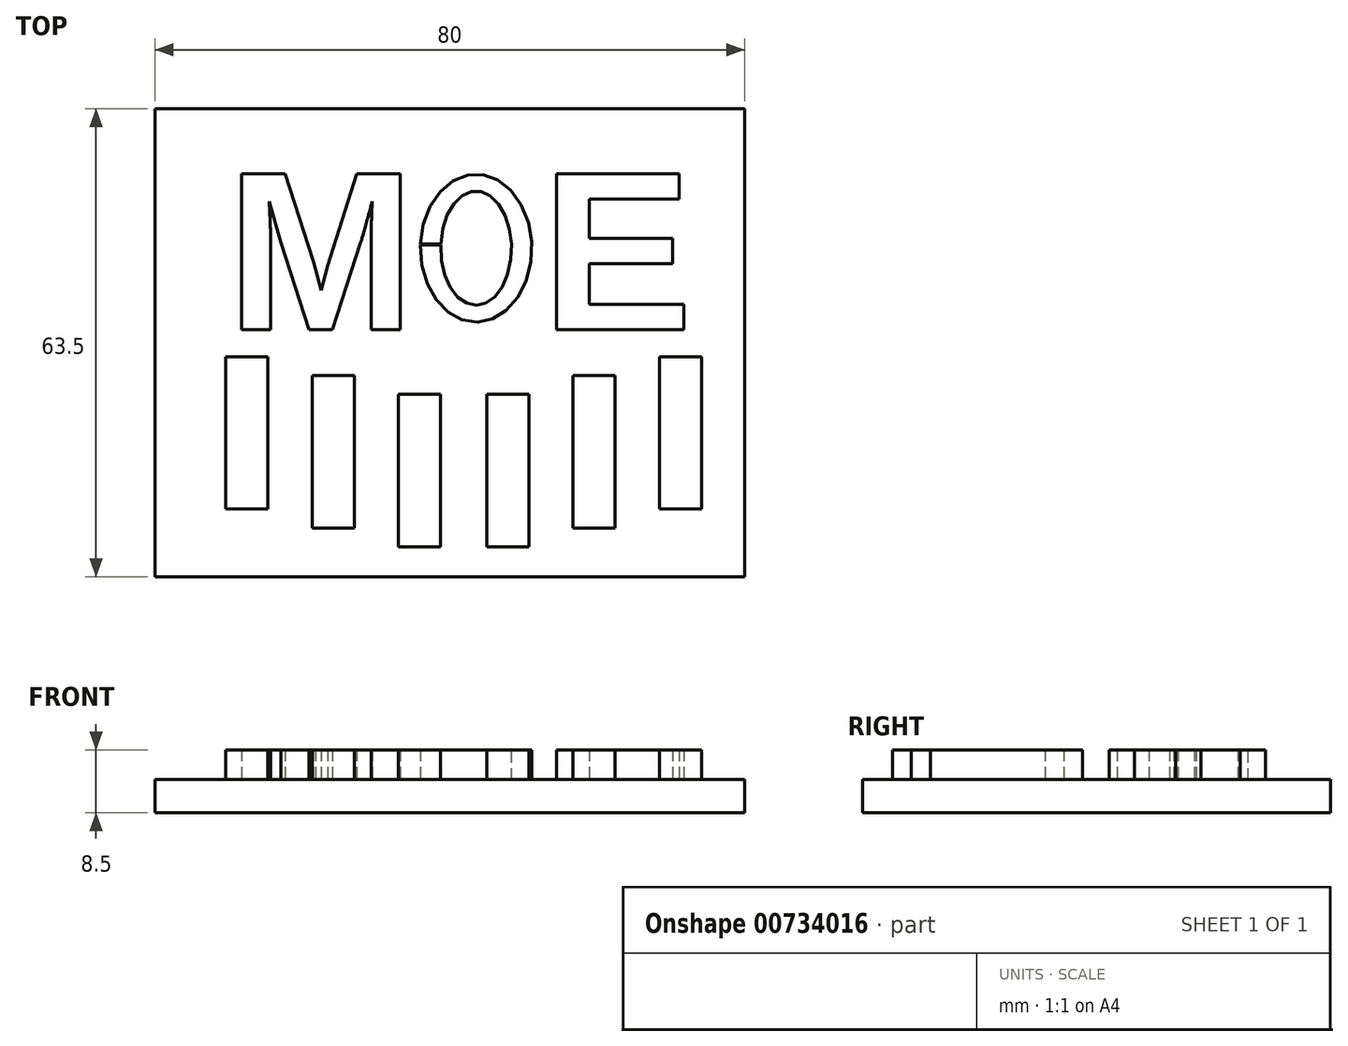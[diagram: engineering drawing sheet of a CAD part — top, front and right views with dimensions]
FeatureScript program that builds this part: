
annotation { "Feature Type Name" : "Feature", "Feature Type Description" : "" }
export const myFeature = defineFeature(function(context is Context, id is Id, definition is map)
    precondition{}
    {
        {
            var Q0;
            Q0=qCreatedBy(makeId("Top.planeOp"),FACE);
            var sketch = newSketch(context, id + "F0", { "sketchPlane" : qUnion([Q0])});
            skLineSegment(sketch, "E0.bottom", {"start": v(40, -33.5) * mm, "end": v(-40, -33.5) * mm});
            skLineSegment(sketch, "E0.top", {"start": v(40, 30) * mm, "end": v(-40, 30) * mm});
            skLineSegment(sketch, "E0.left", {"start": v(40, -30) * mm, "end": v(40, 30) * mm});
            skLineSegment(sketch, "E0.right", {"start": v(-40, -30) * mm, "end": v(-40, 30) * mm});
            skPoint(sketch, "E0.middle", {"position": v(0, 0) * mm});
            skLineSegment(sketch, "E1", {"start": v(-40, -32.5) * mm, "end": v(-40, -30) * mm});
            skLineSegment(sketch, "E2", {"start": v(40, -32.5) * mm, "end": v(40, -30) * mm});
            skLineSegment(sketch, "E3", {"start": v(-40, -33.5) * mm, "end": v(-40, -32.5) * mm});
            skLineSegment(sketch, "E4", {"start": v(40, -33.5) * mm, "end": v(40, -32.5) * mm});
            skSolve(sketch);
        }
        {
            var Q0;
            Q0=qCreatedBy(makeId("Top.planeOp"),FACE);
            var sketch = newSketch(context, id + "F1", { "sketchPlane" : qUnion([Q0])});
            skLineSegment(sketch, "E5.bottom", {"start": v(37, 29.06) * mm, "end": v(-37, 29.06) * mm});
            skLineSegment(sketch, "E5.top", {"start": v(37, -33.44) * mm, "end": v(-37, -33.44) * mm});
            skLineSegment(sketch, "E5.left", {"start": v(39.5, 29.06) * mm, "end": v(39.5, -30.94) * mm});
            skLineSegment(sketch, "E5.right", {"start": v(-39.5, 29.06) * mm, "end": v(-39.5, -30.94) * mm});
            skEllipticalArc(sketch, "E6", {});
            skEllipticalArc(sketch, "E7", {});
            skLineSegment(sketch, "E8", {"start": v(-4, 11.66) * mm, "end": v(-1.23, 11.66) * mm});
            skLineSegment(sketch, "E9", {"start": v(-4, 11.5) * mm, "end": v(-1.24, 11.5) * mm});
            skPoint(sketch, "E10", {"position": v(-2.7, -4.34) * mm});
            skLineSegment(sketch, "E11", {"start": v(-39.5, 29.06) * mm, "end": v(-37, 29.06) * mm});
            skLineSegment(sketch, "E12", {"start": v(37, 29.06) * mm, "end": v(39.5, 29.06) * mm});
            skLineSegment(sketch, "E13", {"start": v(39.5, -30.94) * mm, "end": v(39.5, -33.44) * mm});
            skLineSegment(sketch, "E14", {"start": v(39.5, -33.44) * mm, "end": v(37, -33.44) * mm});
            skLineSegment(sketch, "E15", {"start": v(-39.5, -30.94) * mm, "end": v(-39.5, -33.44) * mm});
            skLineSegment(sketch, "E16", {"start": v(-39.5, -33.44) * mm, "end": v(-37, -33.44) * mm});
            skText(sketch, "E17", { "text": "M  E", "fontName": "Arimo-Bold.ttf"});
            skLineSegment(sketch, "E18.bottom", {"start": v(-24.68, -24.3) * mm, "end": v(-30.4, -24.3) * mm});
            skLineSegment(sketch, "E18.top", {"start": v(-24.68, -3.67) * mm, "end": v(-30.4, -3.67) * mm});
            skLineSegment(sketch, "E18.left", {"start": v(-24.68, -24.3) * mm, "end": v(-24.68, -3.67) * mm});
            skLineSegment(sketch, "E18.right", {"start": v(-30.4, -24.3) * mm, "end": v(-30.4, -3.67) * mm});
            skPoint(sketch, "E18.middle", {"position": v(-27.54, -13.98) * mm});
            skLineSegment(sketch, "E19.bottom", {"start": v(-12.96, -26.9) * mm, "end": v(-18.68, -26.9) * mm});
            skLineSegment(sketch, "E19.top", {"start": v(-12.96, -6.17) * mm, "end": v(-18.68, -6.17) * mm});
            skLineSegment(sketch, "E19.left", {"start": v(-12.96, -26.9) * mm, "end": v(-12.96, -6.17) * mm});
            skLineSegment(sketch, "E19.right", {"start": v(-18.68, -26.9) * mm, "end": v(-18.68, -6.17) * mm});
            skPoint(sketch, "E19.middle", {"position": v(-15.82, -16.53) * mm});
            skLineSegment(sketch, "E20.bottom", {"start": v(-1.25, -29.45) * mm, "end": v(-6.96, -29.45) * mm});
            skLineSegment(sketch, "E20.top", {"start": v(-1.25, -8.73) * mm, "end": v(-6.96, -8.73) * mm});
            skLineSegment(sketch, "E20.left", {"start": v(-1.25, -29.45) * mm, "end": v(-1.25, -8.73) * mm});
            skLineSegment(sketch, "E20.right", {"start": v(-6.96, -29.45) * mm, "end": v(-6.96, -8.73) * mm});
            skPoint(sketch, "E20.middle", {"position": v(-4.1, -19.09) * mm});
            skLineSegment(sketch, "E21.MirrorCS", {"start": v(28.44, -3.67) * mm, "end": v(34.15, -3.67) * mm});
            skLineSegment(sketch, "E22.MirrorCS", {"start": v(28.44, -24.3) * mm, "end": v(28.44, -3.67) * mm});
            skPoint(sketch, "E23.MirrorP", {"position": v(6.46, -4.34) * mm});
            skLineSegment(sketch, "E24.MirrorCS", {"start": v(16.72, -26.9) * mm, "end": v(16.72, -6.17) * mm});
            skLineSegment(sketch, "E25.MirrorCS", {"start": v(5, -29.45) * mm, "end": v(5, -8.73) * mm});
            skLineSegment(sketch, "E26.MirrorCS", {"start": v(5, -8.73) * mm, "end": v(10.72, -8.73) * mm});
            skLineSegment(sketch, "E27.MirrorCS", {"start": v(16.72, -6.17) * mm, "end": v(22.44, -6.17) * mm});
            skLineSegment(sketch, "E28.MirrorCS", {"start": v(16.72, -26.9) * mm, "end": v(22.44, -26.9) * mm});
            skLineSegment(sketch, "E29.MirrorCS", {"start": v(22.44, -26.9) * mm, "end": v(22.44, -6.17) * mm});
            skPoint(sketch, "E30.MirrorP", {"position": v(19.58, -16.53) * mm});
            skLineSegment(sketch, "E31.MirrorCS", {"start": v(34.15, -24.3) * mm, "end": v(34.15, -3.67) * mm});
            skLineSegment(sketch, "E32.MirrorCS", {"start": v(10.72, -29.45) * mm, "end": v(10.72, -8.73) * mm});
            skLineSegment(sketch, "E33.MirrorCS", {"start": v(5, -29.45) * mm, "end": v(10.72, -29.45) * mm});
            skLineSegment(sketch, "E34.MirrorCS", {"start": v(28.44, -24.3) * mm, "end": v(34.15, -24.3) * mm});
            skPoint(sketch, "E35.MirrorP", {"position": v(7.86, -19.09) * mm});
            skPoint(sketch, "E36.MirrorP", {"position": v(31.3, -13.98) * mm});
            const initialGuessF1  = {"E6": [0.0035593705279581347, 0.011075022630393505, 0, -1, 0.010015109553933144, 0.007566245832075456, 4.669752922945587, 4.654139303713688], "E7": [0.0035593705279581347, 0.011075022630393505, 0, -1, 0.007730962708592415, 0.0048037835103717265, 4.657144549083569, 4.636900170979201], "E17": [-0.03033, 0, 1, 0, 0.02216]};
            skSetInitialGuess(sketch, initialGuessF1);
            skSolve(sketch);
        }
        {
            var Q0;
            Q0=makeQuery(id+"F1.imprint","IMPRINT",FACE,{"disambiguationData":[TD([[makeQuery(id+"F1.imprint","IMPRINT",EDGE,{"derivedFrom":sQuery(id+"F1.wireOp",EDGE,"E17.sketch_text.stroke-0")}),-1.0]])]});
            var Q1;
            Q1=makeQuery(id+"F1.imprint","IMPRINT",FACE,{"disambiguationData":[TD([[makeQuery(id+"F1.imprint","IMPRINT",EDGE,{"derivedFrom":sQuery(id+"F1.wireOp",EDGE,"E6")}),1.0]])]});
            var Q2;
            Q2=makeQuery(id+"F1.imprint","IMPRINT",FACE,{"disambiguationData":[TD([[makeQuery(id+"F1.imprint","IMPRINT",EDGE,{"derivedFrom":sQuery(id+"F1.wireOp",EDGE,"E17.sketch_text.stroke-21")}),-1.0]])]});
            var Q3;
            Q3=makeQuery(id+"F1.imprint","IMPRINT",FACE,{"disambiguationData":[TD([[makeQuery(id+"F1.imprint","IMPRINT",EDGE,{"derivedFrom":sQuery(id+"F1.wireOp",EDGE,"E18.bottom")}),-1.0]])]});
            var Q4;
            Q4=makeQuery(id+"F1.imprint","IMPRINT",FACE,{"disambiguationData":[TD([[makeQuery(id+"F1.imprint","IMPRINT",EDGE,{"derivedFrom":sQuery(id+"F1.wireOp",EDGE,"E19.bottom")}),-1.0]])]});
            var Q5;
            Q5=makeQuery(id+"F1.imprint","IMPRINT",FACE,{"disambiguationData":[TD([[makeQuery(id+"F1.imprint","IMPRINT",EDGE,{"derivedFrom":sQuery(id+"F1.wireOp",EDGE,"E20.bottom")}),-1.0]])]});
            var Q6;
            Q6=makeQuery(id+"F1.imprint","IMPRINT",FACE,{"disambiguationData":[TD([[makeQuery(id+"F1.imprint","IMPRINT",EDGE,{"derivedFrom":sQuery(id+"F1.wireOp",EDGE,"E25.MirrorCS")}),-1.0]])]});
            var Q7;
            Q7=makeQuery(id+"F1.imprint","IMPRINT",FACE,{"disambiguationData":[TD([[makeQuery(id+"F1.imprint","IMPRINT",EDGE,{"derivedFrom":sQuery(id+"F1.wireOp",EDGE,"E24.MirrorCS")}),-1.0]])]});
            var Q8;
            Q8=makeQuery(id+"F1.imprint","IMPRINT",FACE,{"disambiguationData":[TD([[makeQuery(id+"F1.imprint","IMPRINT",EDGE,{"derivedFrom":sQuery(id+"F1.wireOp",EDGE,"E21.MirrorCS")}),-1.0]])]});
            extrude(context, id + "F2", {"entities" : qUnion([Q0, Q1, Q2, Q3, Q4, Q5, Q6, Q7, Q8]), "depth" : 8.5 * mm, "offsetDistance" : 25 * mm});
        }
        {
            var Q0;
            Q0 = qSketchRegion(id + "F0", true);
            extrude(context, id + "F3", {"entities" : qUnion([Q0]), "operationType" : NewBodyOperationType.ADD, "depth" : 4.5 * mm, "offsetDistance" : 25 * mm});
        }
    });
